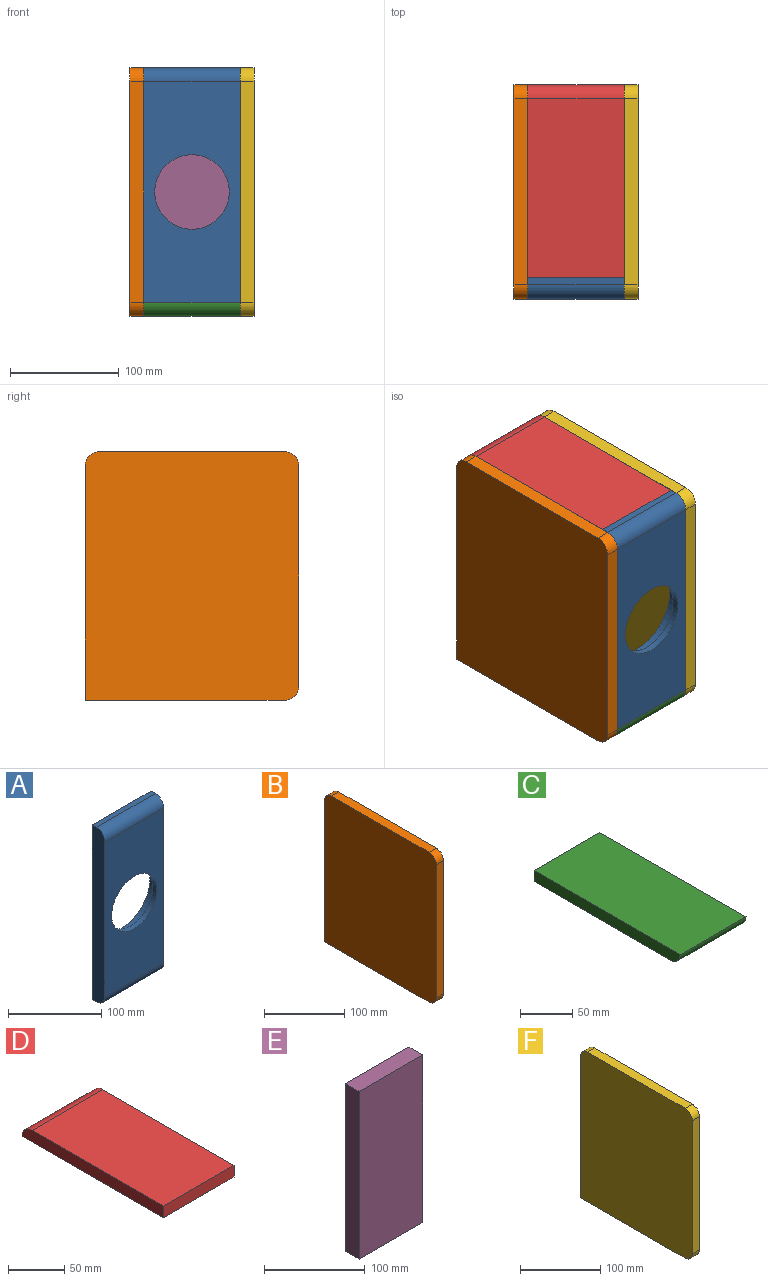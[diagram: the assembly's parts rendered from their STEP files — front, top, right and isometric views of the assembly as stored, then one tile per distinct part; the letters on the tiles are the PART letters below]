
ASSEMBLY  parts=6 mates=16
PART A: 11 faces, bbox 88.9x19.1x228.6 mm
  f0: plane 88.9x6.35mm, normal (0,0,-1), area 564.5mm2, adj f1,f4,f5,f7
  f1: plane 228.6x88.9mm, normal (0,1,0), area 14550.8mm2, adj f0,f2,f4,f5,f10
  f2: plane 88.9x6.35mm, normal (0,0,1), area 564.5mm2, adj f1,f4,f5,f6
  f3: plane 203.2x88.9mm, normal (0,-1,0), area 14370.6mm2, adj f4,f5,f6,f7,f8
  f4: plane 228.6x19.05mm, normal (1,0,0), area 4285.6mm2, adj f0,f1,f2,f3,f6,f7
  f5: plane 228.6x19.05mm, normal (-1,0,0), area 4285.6mm2, adj f0,f1,f2,f3,f6,f7
  f6: cylinder r=12.7mm len=88.9mm, axis (-1,0,0), area 1773.5mm2, adj f2,f3,f4,f5
  f7: cylinder r=12.7mm len=88.9mm, axis (-1,0,0), area 1773.5mm2, adj f0,f3,f4,f5
  f8: cylinder r=34.29mm len=68.58mm, axis (0,1,0), area 1368.1mm2, adj f3,f9
  f9: plane 85.73x85.73mm, normal (0,1,0), area 2077.8mm2, adj f8,f10
  f10: cylinder r=42.86mm len=85.73mm, axis (0,1,0), area 3420.3mm2, adj f1,f9
PART B: 9 faces, bbox 12.7x196.9x228.6 mm
  f0: plane 184.15x12.7mm, normal (0,0,-1), area 2338.7mm2, adj f1,f4,f5,f8
  f1: plane 215.9x12.7mm, normal (0,1,0), area 2741.9mm2, adj f0,f4,f5,f6
  f2: plane 171.45x12.7mm, normal (0,0,1), area 2177.4mm2, adj f4,f5,f6,f7
  f3: plane 203.2x12.7mm, normal (0,-1,0), area 2580.6mm2, adj f4,f5,f7,f8
  f4: plane 228.6x196.85mm, normal (1,0,0), area 44896.1mm2, adj f0,f1,f2,f3,f6,f7,f8
  f5: plane 228.6x196.85mm, normal (-1,0,0), area 44896.1mm2, adj f0,f1,f2,f3,f6,f7,f8
  f6: cylinder r=12.7mm len=12.7mm, axis (-1,0,0), area 253.4mm2, adj f1,f2,f4,f5
  f7: cylinder r=12.7mm len=12.7mm, axis (-1,0,0), area 253.4mm2, adj f2,f3,f4,f5
  f8: cylinder r=12.7mm len=12.7mm, axis (-1,0,0), area 253.4mm2, adj f0,f3,f4,f5
PART C: 6 faces, bbox 88.9x196.9x12.7 mm
  f0: plane 184.15x88.9mm, normal (0,0,-1), area 16370.9mm2, adj f1,f3,f4,f5
  f1: plane 88.9x12.7mm, normal (0,1,0), area 1129mm2, adj f0,f2,f3,f4
  f2: plane 196.85x88.9mm, normal (0,0,1), area 17500mm2, adj f1,f3,f4,f5
  f3: plane 196.85x12.7mm, normal (1,0,0), area 2465.4mm2, adj f0,f1,f2,f5
  f4: plane 196.85x12.7mm, normal (-1,0,0), area 2465.4mm2, adj f0,f1,f2,f5
  f5: cylinder r=12.7mm len=88.9mm, axis (-1,0,0), area 1773.5mm2, adj f0,f2,f3,f4
PART D: 6 faces, bbox 88.9x177.8x12.7 mm
  f0: plane 177.8x88.9mm, normal (0,0,-1), area 15806.4mm2, adj f2,f3,f4,f5
  f1: plane 165.1x88.9mm, normal (0,0,1), area 14677.4mm2, adj f2,f3,f4,f5
  f2: plane 88.9x12.7mm, normal (0,-1,0), area 1129mm2, adj f0,f1,f3,f4
  f3: plane 177.8x12.7mm, normal (1,0,0), area 2223.4mm2, adj f0,f1,f2,f5
  f4: plane 177.8x12.7mm, normal (-1,0,0), area 2223.4mm2, adj f0,f1,f2,f5
  f5: cylinder r=12.7mm len=88.9mm, axis (-1,0,0), area 1773.5mm2, adj f0,f1,f3,f4
PART E: 6 faces, bbox 88.9x19.1x203.2 mm
  f0: plane 88.9x19.05mm, normal (0,0,-1), area 1693.5mm2, adj f1,f3,f4,f5
  f1: plane 203.2x88.9mm, normal (0,1,0), area 18064.5mm2, adj f0,f2,f4,f5
  f2: plane 88.9x19.05mm, normal (0,0,1), area 1693.5mm2, adj f1,f3,f4,f5
  f3: plane 203.2x88.9mm, normal (0,-1,0), area 18064.5mm2, adj f0,f2,f4,f5
  f4: plane 203.2x19.05mm, normal (1,0,0), area 3871mm2, adj f0,f1,f2,f3
  f5: plane 203.2x19.05mm, normal (-1,0,0), area 3871mm2, adj f0,f1,f2,f3
PART F: 9 faces, bbox 12.7x196.9x228.6 mm
  f0: plane 203.2x12.7mm, normal (0,-1,0), area 2580.6mm2, adj f4,f5,f6,f8
  f1: plane 184.15x12.7mm, normal (0,0,-1), area 2338.7mm2, adj f2,f4,f5,f6
  f2: plane 215.9x12.7mm, normal (0,1,0), area 2741.9mm2, adj f1,f4,f5,f7
  f3: plane 171.45x12.7mm, normal (0,0,1), area 2177.4mm2, adj f4,f5,f7,f8
  f4: plane 228.6x196.85mm, normal (1,0,0), area 44896.1mm2, adj f0,f1,f2,f3,f6,f7,f8
  f5: plane 228.6x196.85mm, normal (-1,0,0), area 44896.1mm2, adj f0,f1,f2,f3,f6,f7,f8
  f6: cylinder r=12.7mm len=12.7mm, axis (-1,0,0), area 253.4mm2, adj f0,f1,f4,f5
  f7: cylinder r=12.7mm len=12.7mm, axis (-1,0,0), area 253.4mm2, adj f2,f3,f4,f5
  f8: cylinder r=12.7mm len=12.7mm, axis (-1,0,0), area 253.4mm2, adj f0,f3,f4,f5
PLACE A t=(19.71,187.41,81.62)mm
PLACE B t=(7.01,78.99,-32.68)mm
PLACE C t=(19.71,78.99,-32.68)mm
PLACE D t=(19.71,98.04,183.22)mm
PLACE E t=(19.71,365.21,94.32)mm
PLACE F t=(108.61,78.8,-32.68)mm
MATE planar A.f4 <-> F.f5  axis (1,0,0) through (108.61,88.62,81.62)mm
MATE planar C.f3 <-> F.f5  axis (1,0,0) through (108.61,178.75,-26.28)mm
MATE planar B.f4 <-> E.f5  axis (1,0,0) through (19.71,177.48,81.54)mm
MATE planar D.f3 <-> F.f5  axis (1,0,0) through (108.61,185.6,189.52)mm
MATE parallel B.f4 <-> F.f5  axis (1,0,0) through (19.71,177.48,81.54)mm
MATE planar C.f0 <-> F.f1  axis (0,0,-1) through (64.16,183.76,-32.68)mm
MATE planar A.f2 <-> B.f2  axis (0,0,1) through (64.16,98.04,195.92)mm
MATE planar C.f2 <-> E.f0  axis (0,0,1) through (64.16,177.41,-19.98)mm
MATE planar E.f1 <-> F.f2  axis (0,1,0) through (64.16,275.84,81.62)mm
MATE planar B.f3 <-> F.f0  axis (0,-1,0) through (13.36,78.99,81.62)mm
MATE planar D.f2 <-> A.f8  axis (0,-1,0) through (64.16,98.04,195.92)mm
MATE planar B.f2 <-> F.f3  axis (0,0,1) through (13.36,177.41,195.92)mm
MATE planar C.f1 <-> B.f1  axis (0,1,0) through (64.16,275.84,-26.33)mm
MATE planar D.f1 <-> B.f2  axis (0,0,1) through (64.16,180.59,195.92)mm
MATE planar A.f5 <-> B.f4  axis (-1,0,0) through (19.71,88.62,81.62)mm
MATE planar A.f8 <-> F.f0  axis (0,-1,0) through (64.16,78.99,81.62)mm
